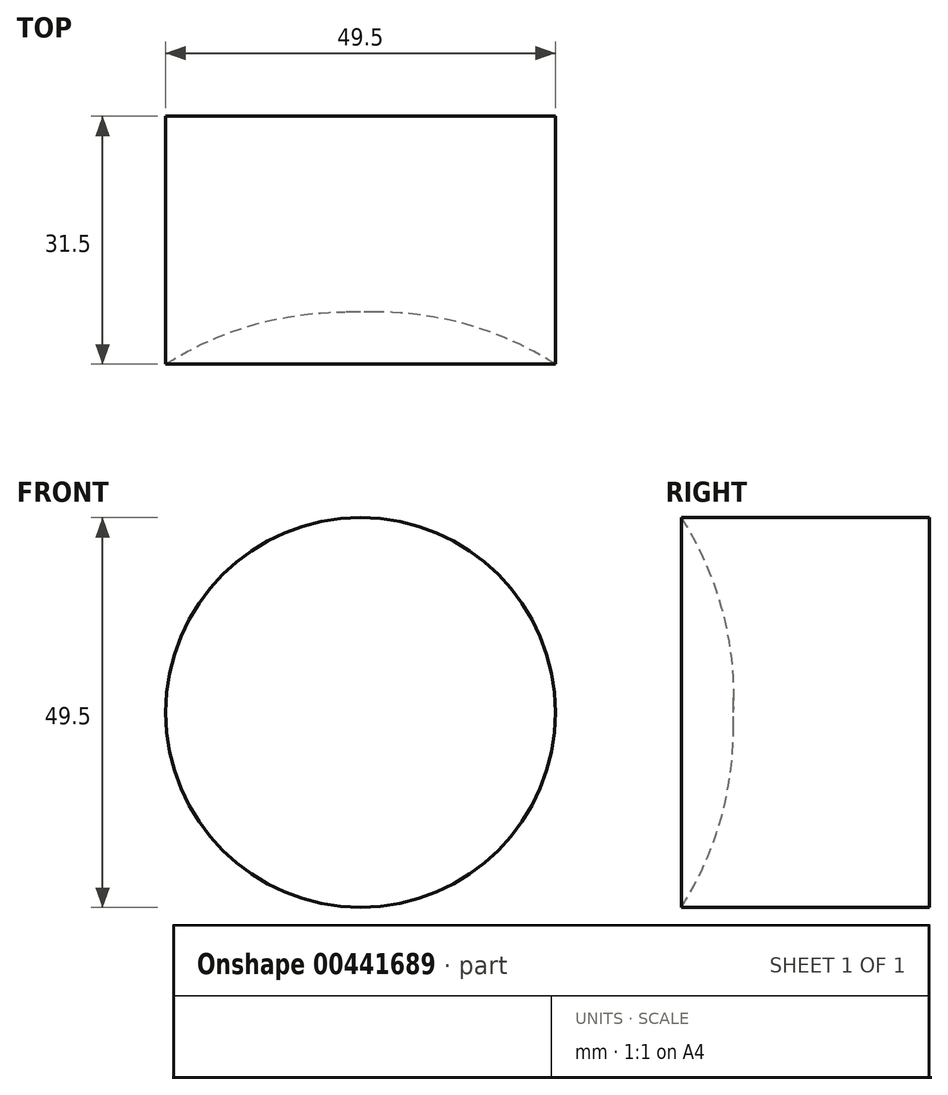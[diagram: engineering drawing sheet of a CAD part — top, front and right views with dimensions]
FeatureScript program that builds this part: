
annotation { "Feature Type Name" : "Feature", "Feature Type Description" : "" }
export const myFeature = defineFeature(function(context is Context, id is Id, definition is map)
    precondition{}
    {
        {
            var Q0;
            Q0=qCreatedBy(makeId("Top.planeOp"),FACE);
            var sketch = newSketch(context, id + "F0", { "sketchPlane" : qUnion([Q0])});
            skLineSegment(sketch, "E0", {"start": v(0, 35.58) * mm, "end": v(24.75, 35.58) * mm});
            skLineSegment(sketch, "E1", {"start": v(24.75, 35.58) * mm, "end": v(24.75, 4.08) * mm});
            skArc(sketch, "E2", {"start": v(0, -74.1) * mm, "mid": v(42.41, -44.52) * mm, "end": v(24.75, 4.08) * mm});
            skLineSegment(sketch, "E3", {"start": v(0, -87.33) * mm, "end": v(0, -90.22) * mm});
            skPoint(sketch, "E4.orphan", {"position": v(0, 68.52) * mm});
            skLineSegment(sketch, "E5", {"start": v(0, 35.58) * mm, "end": v(0, -74.1) * mm});
            skLineSegment(sketch, "E6", {"start": v(0, 61.93) * mm, "end": v(0, -80.86) * mm});
            skSolve(sketch);
        }
        {
            var Q0;
            {var subQ0=sQuery(id+"F0.wireOp",EDGE,"E0");Q0=makeQuery(id+"F0.imprint","IMPRINT",FACE,{"disambiguationData":[TD([[makeQuery(id+"F0.imprint","IMPRINT",EDGE,{"derivedFrom":subQ0}),-1.0]])]});}
            var Q1;
            Q1=sQuery(id+"F0.wireOp",EDGE,"E6");
            revolve(context, id + "F1", {"entities" : qUnion([Q0]), "axis" : qUnion([Q1]), "revolveType" : RevolveType.FULL});
        }
    });
